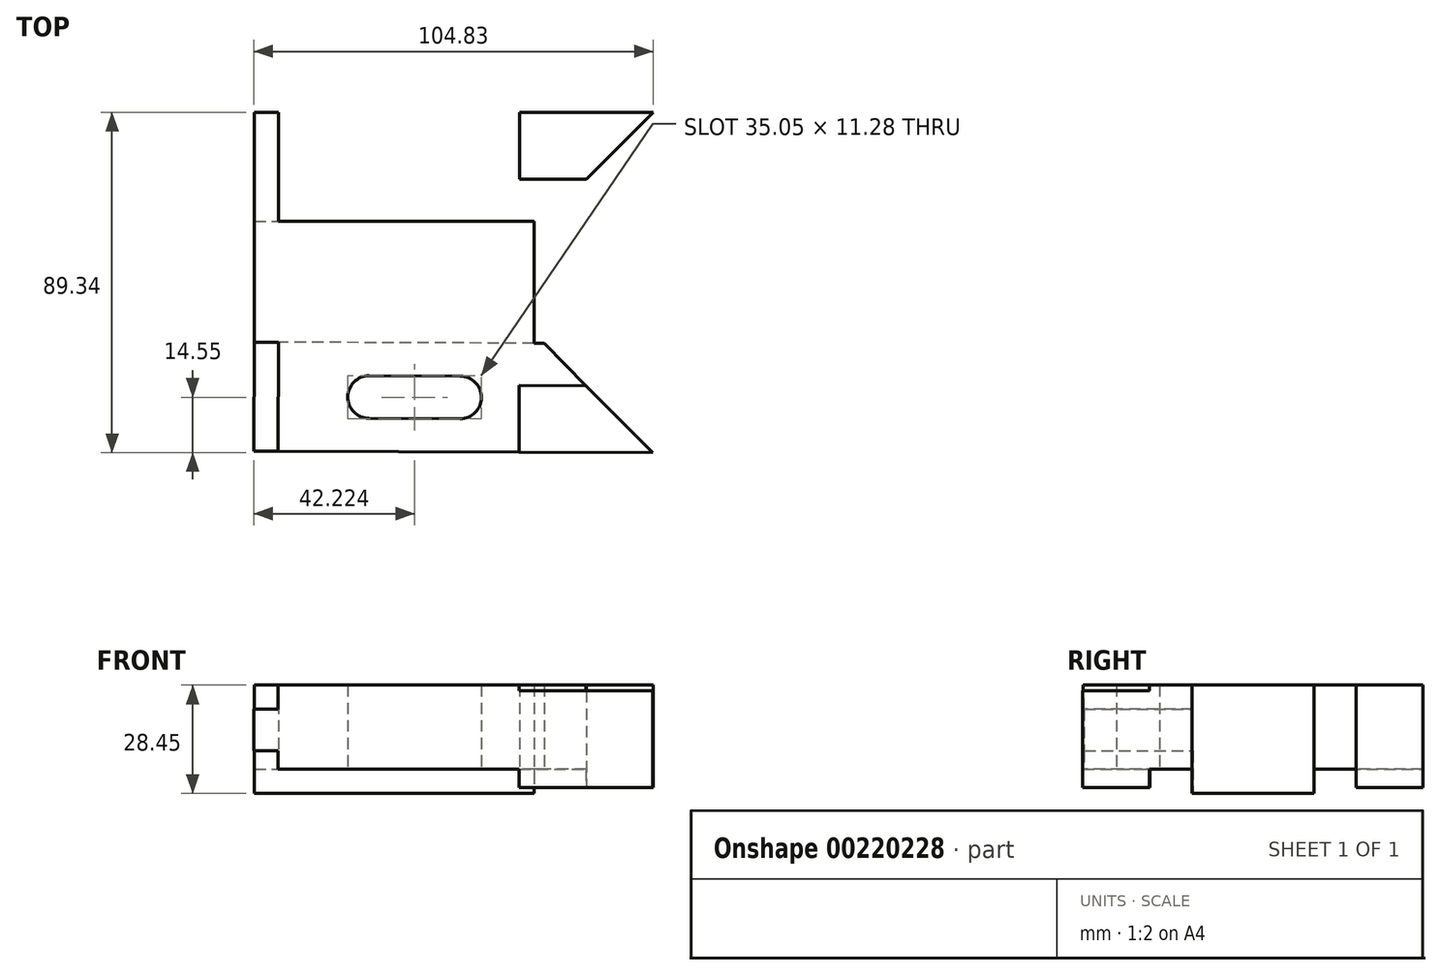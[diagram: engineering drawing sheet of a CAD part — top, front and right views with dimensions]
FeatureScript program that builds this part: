
annotation { "Feature Type Name" : "Feature", "Feature Type Description" : "" }
export const myFeature = defineFeature(function(context is Context, id is Id, definition is map)
    precondition{}
    {
        {
            var Q0;
            Q0=qCreatedBy(makeId("Top.planeOp"),FACE);
            var sketch = newSketch(context, id + "F0", { "sketchPlane" : qUnion([Q0])});
            skLineSegment(sketch, "E0.top", {"start": v(0.19, 88.9) * mm, "end": v(104.83, 88.9) * mm});
            skLineSegment(sketch, "E0.left", {"start": v(0.19, 44.45) * mm, "end": v(0.19, 88.9) * mm});
            skLineSegment(sketch, "E1.bottom", {"start": v(0.19, 60.32) * mm, "end": v(73.6, 60.32) * mm});
            skLineSegment(sketch, "E1.left", {"start": v(0.19, 60.32) * mm, "end": v(0.19, 44.45) * mm});
            skLineSegment(sketch, "E1.right", {"start": v(73.6, 60.32) * mm, "end": v(73.6, 44.3) * mm});
            skLineSegment(sketch, "E2.bottom", {"start": v(0.19, 88.9) * mm, "end": v(6.54, 88.9) * mm});
            skLineSegment(sketch, "E2.top", {"start": v(0.19, 60.32) * mm, "end": v(6.54, 60.32) * mm});
            skLineSegment(sketch, "E2.left", {"start": v(0.19, 88.9) * mm, "end": v(0.19, 60.32) * mm});
            skLineSegment(sketch, "E2.right", {"start": v(6.54, 88.9) * mm, "end": v(6.54, 60.32) * mm});
            skLineSegment(sketch, "E3", {"start": v(104.83, 88.9) * mm, "end": v(76.26, 60.32) * mm});
            skLineSegment(sketch, "E4", {"start": v(76.26, 60.32) * mm, "end": v(73.6, 60.32) * mm});
            skLineSegment(sketch, "E5", {"start": v(69.78, 88.9) * mm, "end": v(69.78, 71.37) * mm});
            skLineSegment(sketch, "E6", {"start": v(69.78, 71.37) * mm, "end": v(87.3, 71.37) * mm});
            skLineSegment(sketch, "E7", {"start": v(0.19, 44.45) * mm, "end": v(73.6, 44.3) * mm, "construction": true});
            skArc(sketch, "E8", {"start": v(30.41, 80.2) * mm, "mid": v(24.82, 74.61) * mm, "end": v(30.41, 69.02) * mm});
            skPoint(sketch, "E8.centerSnap0", {"position": v(6.54, 74.61) * mm});
            skArc(sketch, "E9", {"start": v(54.29, 69.02) * mm, "mid": v(59.88, 74.61) * mm, "end": v(54.29, 80.2) * mm});
            skLineSegment(sketch, "E10", {"start": v(30.41, 80.2) * mm, "end": v(54.29, 80.2) * mm});
            skLineSegment(sketch, "E11", {"start": v(54.29, 69.02) * mm, "end": v(30.41, 69.02) * mm});
            skLineSegment(sketch, "E12.MirrorCS", {"start": v(0.12, 28.57) * mm, "end": v(0.19, 44.45) * mm});
            skLineSegment(sketch, "E13.MirrorCS", {"start": v(0, 0) * mm, "end": v(0.12, 28.57) * mm});
            skLineSegment(sketch, "E14.MirrorCS", {"start": v(0, 0) * mm, "end": v(6.35, -0.03) * mm});
            skLineSegment(sketch, "E15.MirrorCS", {"start": v(6.35, -0.03) * mm, "end": v(6.47, 28.55) * mm});
            skLineSegment(sketch, "E16.MirrorCS", {"start": v(0, 0) * mm, "end": v(104.65, -0.44) * mm});
            skLineSegment(sketch, "E17.MirrorCS", {"start": v(104.65, -0.44) * mm, "end": v(76.2, 28.25) * mm});
            skLineSegment(sketch, "E18.MirrorCS", {"start": v(76.2, 28.25) * mm, "end": v(73.53, 28.27) * mm});
            skLineSegment(sketch, "E19.MirrorCS", {"start": v(73.53, 28.27) * mm, "end": v(73.6, 44.3) * mm});
            skLineSegment(sketch, "E20.MirrorCS", {"start": v(0.12, 28.57) * mm, "end": v(73.53, 28.27) * mm});
            skArc(sketch, "E21.MirrorCS", {"start": v(30.26, 8.57) * mm, "mid": v(24.7, 14.18) * mm, "end": v(30.3, 19.75) * mm});
            skLineSegment(sketch, "E22.MirrorCS", {"start": v(30.26, 8.57) * mm, "end": v(54.14, 8.47) * mm});
            skArc(sketch, "E23.MirrorCS", {"start": v(54.19, 19.65) * mm, "mid": v(59.75, 14.04) * mm, "end": v(54.14, 8.47) * mm});
            skLineSegment(sketch, "E24.MirrorCS", {"start": v(54.19, 19.65) * mm, "end": v(30.3, 19.75) * mm});
            skLineSegment(sketch, "E25.MirrorCS", {"start": v(69.6, -0.3) * mm, "end": v(69.67, 17.23) * mm});
            skLineSegment(sketch, "E26.MirrorCS", {"start": v(69.67, 17.23) * mm, "end": v(87.2, 17.16) * mm});
            skSolve(sketch);
        }
        {
            var Q0;
            Q0=makeQuery(id+"F0.imprint","IMPRINT",FACE,{"disambiguationData":[TD([[makeQuery(id+"F0.imprint","IMPRINT",EDGE,{"derivedFrom":sQuery(id+"F0.wireOp",EDGE,"E1.bottom")}),-1.0]])]});
            var Q1;
            Q1=makeQuery(id+"F0.imprint","IMPRINT",FACE,{"disambiguationData":[TD([[makeQuery(id+"F0.imprint","IMPRINT",EDGE,{"derivedFrom":sQuery(id+"F0.wireOp",EDGE,"E1.bottom")}),1.0]])]});
            var Q2;
            Q2=makeQuery(id+"F0.imprint","IMPRINT",FACE,{"disambiguationData":[TD([[makeQuery(id+"F0.imprint","IMPRINT",EDGE,{"derivedFrom":sQuery(id+"F0.wireOp",EDGE,"E2.bottom")}),-1.0]])]});
            var Q3;
            {var subQ4=sQuery(id+"F0.wireOp",EDGE,"E15.MirrorCS");Q3=makeQuery(id+"F0.imprint","IMPRINT",FACE,{"disambiguationData":[TD([[makeQuery(id+"F0.imprint","IMPRINT",EDGE,{"derivedFrom":subQ4}),-1.0]])]});}
            var Q4;
            {var subQ3=sQuery(id+"F0.wireOp",EDGE,"E25.MirrorCS");Q4=makeQuery(id+"F0.imprint","IMPRINT",FACE,{"disambiguationData":[TD([[makeQuery(id+"F0.imprint","IMPRINT",EDGE,{"derivedFrom":subQ3}),-1.0]])]});}
            var Q5;
            {var subQ0=sQuery(id+"F0.wireOp",EDGE,"E13.MirrorCS");Q5=makeQuery(id+"F0.imprint","IMPRINT",FACE,{"disambiguationData":[TD([[makeQuery(id+"F0.imprint","IMPRINT",EDGE,{"derivedFrom":subQ0}),-1.0]])]});}
            var Q6;
            {var subQ3=sQuery(id+"F0.wireOp",EDGE,"E5");Q6=makeQuery(id+"F0.imprint","IMPRINT",FACE,{"disambiguationData":[TD([[makeQuery(id+"F0.imprint","IMPRINT",EDGE,{"derivedFrom":subQ3}),1.0]])]});}
            extrude(context, id + "F1", {"entities" : qUnion([Q0, Q1, Q2, Q3, Q4, Q5, Q6]), "depth" : 28.45 * mm});
        }
        {
            var Q0;
            Q0=makeQuery(id+"F1.opExtrude","CAP_FACE",FACE,{"disambiguationData":[OSD([sQuery(id+"F0.wireOp",EDGE,"E0.top"),sQuery(id+"F0.wireOp",EDGE,"E1.left"),sQuery(id+"F0.wireOp",EDGE,"E1.right"),sQuery(id+"F0.wireOp",EDGE,"E2.bottom"),sQuery(id+"F0.wireOp",EDGE,"E2.left"),sQuery(id+"F0.wireOp",EDGE,"E3"),sQuery(id+"F0.wireOp",EDGE,"E4"),sQuery(id+"F0.wireOp",EDGE,"E8"),sQuery(id+"F0.wireOp",EDGE,"E9"),sQuery(id+"F0.wireOp",EDGE,"E10"),sQuery(id+"F0.wireOp",EDGE,"E11"),sQuery(id+"F0.wireOp",EDGE,"E12.MirrorCS"),sQuery(id+"F0.wireOp",EDGE,"E13.MirrorCS"),sQuery(id+"F0.wireOp",EDGE,"E16.MirrorCS"),sQuery(id+"F0.wireOp",EDGE,"E17.MirrorCS"),sQuery(id+"F0.wireOp",EDGE,"E18.MirrorCS"),sQuery(id+"F0.wireOp",EDGE,"E19.MirrorCS"),sQuery(id+"F0.wireOp",EDGE,"E21.MirrorCS"),sQuery(id+"F0.wireOp",EDGE,"E22.MirrorCS"),sQuery(id+"F0.wireOp",EDGE,"E23.MirrorCS"),sQuery(id+"F0.wireOp",EDGE,"E24.MirrorCS")])],"isStart":false});
            var sketch = newSketch(context, id + "F2", { "sketchPlane" : qUnion([Q0])});
            skLineSegment(sketch, "E27.0.0", {"start": v(87.2, 17.16) * mm, "end": v(69.67, 17.23) * mm});
            skLineSegment(sketch, "E27.0.1", {"start": v(69.67, 17.23) * mm, "end": v(69.6, -0.3) * mm});
            skLineSegment(sketch, "E27.0.2", {"start": v(69.6, -0.3) * mm, "end": v(104.65, -0.44) * mm});
            skLineSegment(sketch, "E27.0.3", {"start": v(104.65, -0.44) * mm, "end": v(87.2, 17.16) * mm});
            skLineSegment(sketch, "E28.0.0", {"start": v(104.83, 88.9) * mm, "end": v(69.78, 88.9) * mm});
            skLineSegment(sketch, "E28.0.1", {"start": v(69.78, 88.9) * mm, "end": v(69.78, 71.37) * mm});
            skLineSegment(sketch, "E28.0.2", {"start": v(69.78, 71.37) * mm, "end": v(87.3, 71.37) * mm});
            skLineSegment(sketch, "E28.0.3", {"start": v(87.3, 71.37) * mm, "end": v(104.83, 88.9) * mm});
            skLineSegment(sketch, "E29.0.0", {"start": v(69.6, -0.3) * mm, "end": v(69.67, 17.23) * mm});
            skLineSegment(sketch, "E29.0.1", {"start": v(69.67, 17.23) * mm, "end": v(87.2, 17.16) * mm});
            skLineSegment(sketch, "E29.0.2", {"start": v(87.2, 17.16) * mm, "end": v(76.2, 28.25) * mm});
            skLineSegment(sketch, "E29.0.3", {"start": v(76.2, 28.25) * mm, "end": v(73.53, 28.27) * mm});
            skLineSegment(sketch, "E29.0.4", {"start": v(73.53, 28.27) * mm, "end": v(6.47, 28.55) * mm});
            skLineSegment(sketch, "E29.0.5", {"start": v(6.47, 28.55) * mm, "end": v(6.35, -0.03) * mm});
            skLineSegment(sketch, "E29.0.6", {"start": v(6.35, -0.03) * mm, "end": v(69.6, -0.3) * mm});
            skLineSegment(sketch, "E30.0.0", {"start": v(73.6, 60.32) * mm, "end": v(76.26, 60.32) * mm});
            skLineSegment(sketch, "E30.0.1", {"start": v(76.26, 60.32) * mm, "end": v(87.3, 71.37) * mm});
            skLineSegment(sketch, "E30.0.2", {"start": v(87.3, 71.37) * mm, "end": v(69.78, 71.37) * mm});
            skLineSegment(sketch, "E30.0.3", {"start": v(69.78, 71.37) * mm, "end": v(69.78, 88.9) * mm});
            skLineSegment(sketch, "E30.0.4", {"start": v(69.78, 88.9) * mm, "end": v(6.54, 88.9) * mm});
            skLineSegment(sketch, "E30.0.5", {"start": v(6.54, 88.9) * mm, "end": v(6.54, 60.32) * mm});
            skLineSegment(sketch, "E30.0.6", {"start": v(6.54, 60.32) * mm, "end": v(73.6, 60.32) * mm});
            skLineSegment(sketch, "E31.0.0", {"start": v(6.47, 28.55) * mm, "end": v(0.12, 28.57) * mm});
            skLineSegment(sketch, "E31.0.1", {"start": v(0.12, 28.57) * mm, "end": v(0, 0) * mm});
            skLineSegment(sketch, "E31.0.2", {"start": v(0, 0) * mm, "end": v(6.35, -0.03) * mm});
            skLineSegment(sketch, "E31.0.3", {"start": v(6.35, -0.03) * mm, "end": v(6.47, 28.55) * mm});
            skLineSegment(sketch, "E32.0.0", {"start": v(6.54, 60.32) * mm, "end": v(6.54, 88.9) * mm});
            skLineSegment(sketch, "E32.0.1", {"start": v(6.54, 88.9) * mm, "end": v(0.19, 88.9) * mm});
            skLineSegment(sketch, "E32.0.2", {"start": v(0.19, 88.9) * mm, "end": v(0.19, 60.32) * mm});
            skLineSegment(sketch, "E32.0.3", {"start": v(0.19, 60.32) * mm, "end": v(6.54, 60.32) * mm});
            skSolve(sketch);
        }
        {
            var Q0;
            Q0=makeQuery(id+"F2.imprint","IMPRINT",FACE,{"disambiguationData":[TD([[makeQuery(id+"F2.imprint","IMPRINT",EDGE,{"derivedFrom":sQuery(id+"F2.wireOp",EDGE,"E27.0.0")}),1.0]])]});
            var Q1;
            Q1=makeQuery(id+"F2.imprint","IMPRINT",FACE,{"disambiguationData":[TD([[makeQuery(id+"F2.imprint","IMPRINT",EDGE,{"derivedFrom":sQuery(id+"F2.wireOp",EDGE,"E28.0.0")}),-1.0]])]});
            var Q2;
            Q2=makeQuery(id+"F2.imprint","IMPRINT",FACE,{"disambiguationData":[TD([[makeQuery(id+"F2.imprint","IMPRINT",EDGE,{"derivedFrom":sQuery(id+"F2.wireOp",EDGE,"E27.0.2")}),1.0]])]});
            extrude(context, id + "F3", {"entities" : qUnion([Q0, Q1, Q2]), "operationType" : NewBodyOperationType.REMOVE, "oppositeDirection" : true, "depth" : 1.52 * mm});
        }
        {
            var Q0;
            {var subQ3=sQuery(id+"F0.wireOp",EDGE,"E25.MirrorCS");Q0=makeQuery(id+"F0.imprint","IMPRINT",FACE,{"disambiguationData":[TD([[makeQuery(id+"F0.imprint","IMPRINT",EDGE,{"derivedFrom":subQ3}),-1.0]])]});}
            var Q1;
            {var subQ3=sQuery(id+"F0.wireOp",EDGE,"E5");Q1=makeQuery(id+"F0.imprint","IMPRINT",FACE,{"disambiguationData":[TD([[makeQuery(id+"F0.imprint","IMPRINT",EDGE,{"derivedFrom":subQ3}),1.0]])]});}
            extrude(context, id + "F4", {"entities" : qUnion([Q0, Q1]), "operationType" : NewBodyOperationType.REMOVE, "depth" : 1.52 * mm});
        }
        {
            var Q0;
            {var subQ4=sQuery(id+"F0.wireOp",EDGE,"E15.MirrorCS");Q0=makeQuery(id+"F0.imprint","IMPRINT",FACE,{"disambiguationData":[TD([[makeQuery(id+"F0.imprint","IMPRINT",EDGE,{"derivedFrom":subQ4}),-1.0]])]});}
            var Q1;
            Q1=makeQuery(id+"F0.imprint","IMPRINT",FACE,{"disambiguationData":[TD([[makeQuery(id+"F0.imprint","IMPRINT",EDGE,{"derivedFrom":sQuery(id+"F0.wireOp",EDGE,"E1.bottom")}),1.0]])]});
            var Q2;
            {var subQ0=sQuery(id+"F0.wireOp",EDGE,"E13.MirrorCS");Q2=makeQuery(id+"F0.imprint","IMPRINT",FACE,{"disambiguationData":[TD([[makeQuery(id+"F0.imprint","IMPRINT",EDGE,{"derivedFrom":subQ0}),-1.0]])]});}
            var Q3;
            Q3=makeQuery(id+"F0.imprint","IMPRINT",FACE,{"disambiguationData":[TD([[makeQuery(id+"F0.imprint","IMPRINT",EDGE,{"derivedFrom":sQuery(id+"F0.wireOp",EDGE,"E2.bottom")}),-1.0]])]});
            extrude(context, id + "F5", {"entities" : qUnion([Q0, Q1, Q2, Q3]), "operationType" : NewBodyOperationType.REMOVE, "depth" : 6.35 * mm});
        }
        {
            var Q0;
            {var subQ0=sQuery(id+"F0.wireOp",EDGE,"E13.MirrorCS");Q0=makeQuery(id+"F0.imprint","IMPRINT",FACE,{"disambiguationData":[TD([[makeQuery(id+"F0.imprint","IMPRINT",EDGE,{"derivedFrom":subQ0}),-1.0]])]});}
            var Q1;
            Q1=makeQuery(id+"F0.imprint","IMPRINT",FACE,{"disambiguationData":[TD([[makeQuery(id+"F0.imprint","IMPRINT",EDGE,{"derivedFrom":sQuery(id+"F0.wireOp",EDGE,"E2.bottom")}),-1.0]])]});
            extrude(context, id + "F6", {"entities" : qUnion([Q0, Q1]), "operationType" : NewBodyOperationType.ADD, "depth" : 11.18 * mm});
        }
        {
            var Q0;
            {var subQ0=sQuery(id+"F0.wireOp",EDGE,"E13.MirrorCS");Q0=makeQuery(id+"F0.imprint","IMPRINT",FACE,{"disambiguationData":[TD([[makeQuery(id+"F0.imprint","IMPRINT",EDGE,{"derivedFrom":subQ0}),-1.0]])]});}
            var Q1;
            Q1=makeQuery(id+"F0.imprint","IMPRINT",FACE,{"disambiguationData":[TD([[makeQuery(id+"F0.imprint","IMPRINT",EDGE,{"derivedFrom":sQuery(id+"F0.wireOp",EDGE,"E2.bottom")}),-1.0]])]});
            extrude(context, id + "F7", {"entities" : qUnion([Q0, Q1]), "operationType" : NewBodyOperationType.REMOVE, "depth" : 11.18 * mm});
        }
        {
            var Q0;
            Q0=makeQuery(id+"F2.imprint","IMPRINT",FACE,{"disambiguationData":[TD([[makeQuery(id+"F2.imprint","IMPRINT",EDGE,{"derivedFrom":sQuery(id+"F2.wireOp",EDGE,"E29.0.0")}),1.0]])]});
            var Q1;
            Q1=makeQuery(id+"F2.imprint","IMPRINT",FACE,{"disambiguationData":[TD([[makeQuery(id+"F2.imprint","IMPRINT",EDGE,{"derivedFrom":sQuery(id+"F2.wireOp",EDGE,"E30.0.0")}),-1.0]])]});
            var Q2;
            Q2=makeQuery(id+"F2.imprint","IMPRINT",FACE,{"disambiguationData":[TD([[makeQuery(id+"F2.imprint","IMPRINT",EDGE,{"derivedFrom":sQuery(id+"F2.wireOp",EDGE,"E31.0.0")}),1.0]])]});
            var Q3;
            Q3=makeQuery(id+"F2.imprint","IMPRINT",FACE,{"disambiguationData":[TD([[makeQuery(id+"F2.imprint","IMPRINT",EDGE,{"derivedFrom":sQuery(id+"F2.wireOp",EDGE,"E32.0.0")}),1.0]])]});
            extrude(context, id + "F8", {"entities" : qUnion([Q0, Q1, Q2, Q3]), "operationType" : NewBodyOperationType.REMOVE, "oppositeDirection" : true, "depth" : 6.35 * mm});
        }
    });
